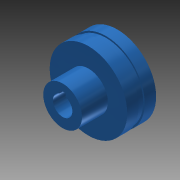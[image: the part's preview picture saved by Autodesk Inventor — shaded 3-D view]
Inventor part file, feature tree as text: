
AUTODESK INVENTOR PART (.ipt)
format: ipt  version: 2014 SP1 (Build 180222100, 222)  size: 121,856 bytes
history: native  units: in
note: dims shown in document units (in); Inventor stores cm internally (conversion verified against a paired STEP export)
features: extrude x6, sketch x6
ambient origin geometry x8: Origin, YZ Plane, XZ Plane, XY Plane, X Axis, Y Axis, Z Axis, Center Point
bodies: Body1 (feature_tree)
feature tree (12):
  extrude  "Extrusion4"  Depth=0.1181in TaperAngle=0.0deg
  extrude  "Extrusion5"  Depth=0.2205in TaperAngle=0.0deg
  extrude  "Extrusion6"  Depth=0.2205in TaperAngle=0.0deg
  extrude  "Extrusion7"  Depth=0.5in TaperAngle=0.0deg
  extrude  "Extrusion8"  Depth=0.375in TaperAngle=0.0deg
  extrude  "Extrusion9"  Depth=0.1153in
  sketch  "Sketch4"  dims[d9=1.4409in d10=0.1181in d11=0.0in]
  sketch  "Sketch5"  dims[d12=1.5in d13=0.2205in d14=0.0in]
  sketch  "Sketch6"  dims[d15=1.5in d16=0.2205in d17=0.0in]
  sketch  "Sketch7"  dims[d18=0.75in d19=0.5in d20=0.0in]
  sketch  "Sketch8"  dims[d21=0.375in d22=1.5in d23=0.0in]
  sketch  "Sketch9"  dims[d24=0.1153in d25=0.1153in d26=0.1265in d27=0.0576in d28=1.5in d29=0.0in]
